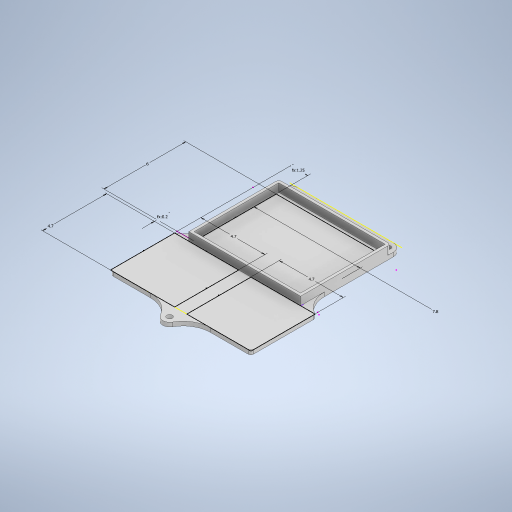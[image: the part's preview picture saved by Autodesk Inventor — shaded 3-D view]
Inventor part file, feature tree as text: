
AUTODESK INVENTOR PART (.ipt)
format: ipt  version: 2024 (Build 280153000, 153)  size: 361,472 bytes
history: native  units: in
note: dims shown in document units (in); Inventor stores cm internally (conversion verified against a paired STEP export)
features: fillet x4, sketch x3, extrude x2
ambient origin geometry x8: Origin, YZ Plane, XZ Plane, XY Plane, X Axis, Y Axis, Z Axis, Center Point
bodies: Solid1 (feature_tree)
feature tree (9):
  extrude  "Extrusion1"  Depth=4.0551in
  sketch  "Sketch2"  dims[d3=3.2283in d4=2.8346in d5=0.4134in d6=0.1575in d7=0.1969in]
  sketch  "Sketch3"  dims[d8=0.1969in d14=0.1969in d15=0.1969in d16=0.1181in d17=0.0in d21=1.8504in d22=1.8504in d26=1.8504in d31=1.8504in d32=1.8504in d33=1.8504in d34=1.8504in d36=0.1969in d37=0.0787in d38=0.0787in d39=3.0709in d40=2.3622in d43=0.4921in d44=3.0709in d45=2.4409in d46=0.4921in d47=1.9291in d48=3.2283in d49=0.0787in d51=2.5984in d52=0.0787in d54=2.0276in d55=0.315in d56=0.3937in d57=0.7874in d58=0.2362in d59=0.0in d61=0.0787in d62=0.7874in d63=0.2362in d64=0.0787in]
  fillet  "Fillet1"  Radius=2.3819in
  extrude  "Extrusion2"  Depth=2.8346in
  fillet  "Fillet3"  Radius=0.4134in
  fillet  "Fillet4"  Radius=0.1575in
  fillet  "Fillet5"  Radius=0.1969in
  sketch  "Sketch1"  dims[d0=4.7638in d1=4.0551in d2=2.3819in]
